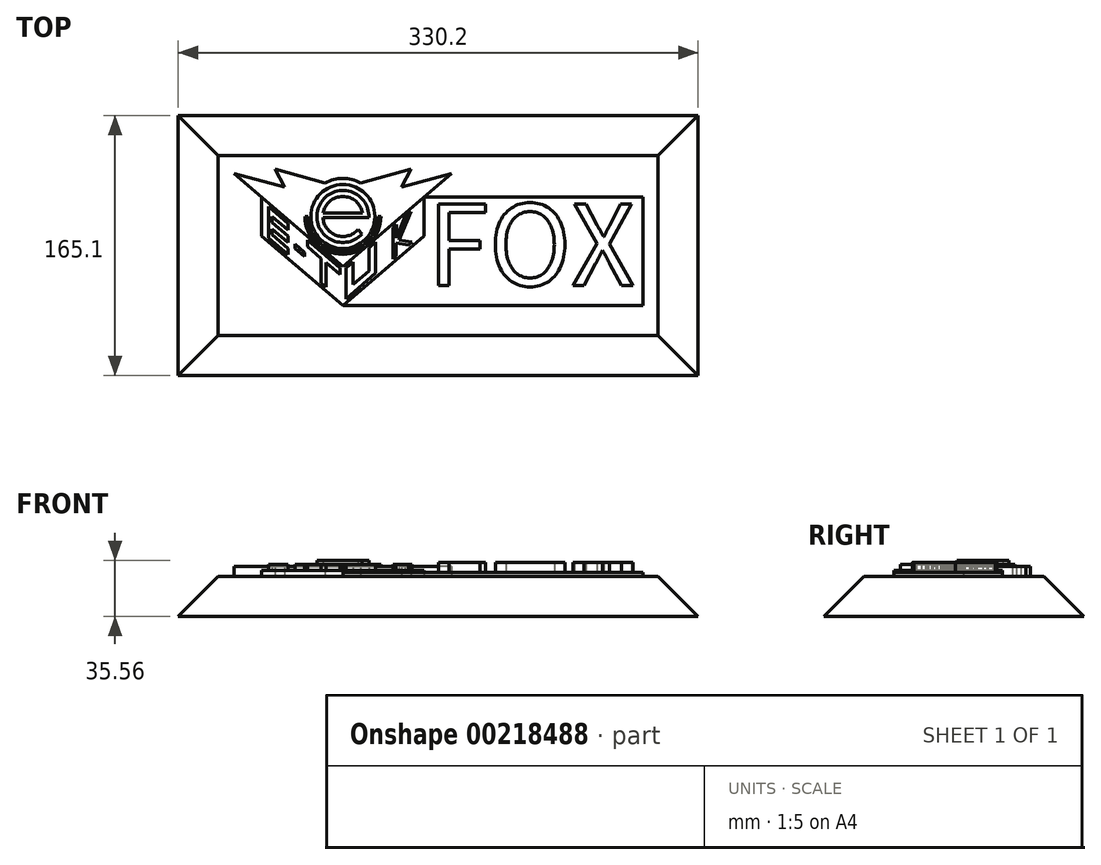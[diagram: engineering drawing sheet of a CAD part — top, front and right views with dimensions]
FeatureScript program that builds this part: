
annotation { "Feature Type Name" : "Feature", "Feature Type Description" : "" }
export const myFeature = defineFeature(function(context is Context, id is Id, definition is map)
    precondition{}
    {
        {
            var Q0;
            Q0=qCreatedBy(makeId("Top.planeOp"),FACE);
            var sketch = newSketch(context, id + "F0", { "sketchPlane" : qUnion([Q0])});
            skArc(sketch, "E0", {"start": v(12.53, 2.07) * mm, "mid": v(0, 12.7) * mm, "end": v(-12.53, 2.07) * mm});
            skArc(sketch, "E1", {"start": v(16.5, -0.78) * mm, "mid": v(-15.23, 6.37) * mm, "end": v(12.14, -11.18) * mm});
            skLineSegment(sketch, "E2", {"start": v(12.7, -0.78) * mm, "end": v(-12.68, -0.78) * mm});
            skLineSegment(sketch, "E3", {"start": v(-12.68, -0.78) * mm, "end": v(16.5, -0.78) * mm});
            skLineSegment(sketch, "E4", {"start": v(9.59, -8.33) * mm, "end": v(12.14, -11.18) * mm});
            skArc(sketch, "E5.trimOffspring", {"start": v(-12.68, -0.78) * mm, "mid": v(-4.08, -12.03) * mm, "end": v(9.59, -8.33) * mm});
            skLineSegment(sketch, "E6", {"start": v(-12.53, 2.07) * mm, "end": v(12.53, 2.07) * mm});
            skSolve(sketch);
        }
        {
            var Q0;
            Q0=makeQuery(id+"F0.imprint","IMPRINT",FACE,{"disambiguationData":[TD([[makeQuery(id+"F0.imprint","IMPRINT",EDGE,{"derivedFrom":sQuery(id+"F0.wireOp",EDGE,"E0")}),-1.0]])]});
            extrude(context, id + "F1", {"entities" : qUnion([Q0]), "depth" : 10.16 * mm});
        }
        {
            var Q0;
            Q0=qCreatedBy(makeId("Top.planeOp"),FACE);
            var sketch = newSketch(context, id + "F2", { "sketchPlane" : qUnion([Q0])});
            skCircle(sketch, "E7", {"center": v(0, 0) * mm, "radius": 20.32 * mm});
            skSolve(sketch);
        }
        {
            var Q0;
            Q0=qSketchRegion(id+"F2",true);
            extrude(context, id + "F3", {"entities" : qUnion([Q0]), "operationType" : NewBodyOperationType.ADD, "depth" : 7.62 * mm});
        }
        {
            var Q0;
            Q0=qCreatedBy(makeId("Top.planeOp"),FACE);
            var sketch = newSketch(context, id + "F4", { "sketchPlane" : qUnion([Q0])});
            skLineSegment(sketch, "E8", {"start": v(-69.02, 27.27) * mm, "end": v(-37.13, 18.72) * mm});
            skLineSegment(sketch, "E9", {"start": v(-37.13, 18.72) * mm, "end": v(-43.14, 30.14) * mm});
            skLineSegment(sketch, "E10", {"start": v(-43.14, 30.14) * mm, "end": v(-11.32, 21.31) * mm});
            skLineSegment(sketch, "E11", {"start": v(-69.02, 27.27) * mm, "end": v(0, -31.75) * mm});
            skLineSegment(sketch, "E12.MirrorCS", {"start": v(43.14, 30.14) * mm, "end": v(11.32, 21.31) * mm});
            skLineSegment(sketch, "E13.MirrorCS", {"start": v(69.02, 27.27) * mm, "end": v(0, -31.75) * mm});
            skLineSegment(sketch, "E14.MirrorCS", {"start": v(69.02, 27.27) * mm, "end": v(37.13, 18.72) * mm});
            skLineSegment(sketch, "E15.MirrorCS", {"start": v(37.13, 18.72) * mm, "end": v(43.14, 30.14) * mm});
            skArc(sketch, "E16.trimOffspring", {"start": v(11.32, 21.31) * mm, "mid": v(0, 24.13) * mm, "end": v(-11.32, 21.31) * mm});
            skSolve(sketch);
        }
        {
            var Q0;
            Q0=qSketchRegion(id+"F4",true);
            var Q1;
            Q1=makeQuery(id+"F2.imprint","IMPRINT",FACE,{"disambiguationData":[TD([[makeQuery(id+"F2.imprint","IMPRINT",EDGE,{"derivedFrom":sQuery(id+"F2.wireOp",EDGE,"E7")}),1.0]])]});
            extrude(context, id + "F5", {"entities" : qUnion([Q0, Q1]), "operationType" : NewBodyOperationType.ADD, "depth" : 6.35 * mm});
        }
        {
            var Q0;
            Q0=qCreatedBy(makeId("Top.planeOp"),FACE);
            var sketch = newSketch(context, id + "F6", { "sketchPlane" : qUnion([Q0])});
            skLineSegment(sketch, "E17", {"start": v(-51.6, -12.38) * mm, "end": v(0, -56.51) * mm});
            skLineSegment(sketch, "E18", {"start": v(0, -56.51) * mm, "end": v(51.6, -12.38) * mm});
            skLineSegment(sketch, "E19", {"start": v(-51.6, 12.38) * mm, "end": v(-51.6, -12.38) * mm});
            skLineSegment(sketch, "E20", {"start": v(51.6, 12.38) * mm, "end": v(51.6, -12.38) * mm});
            skLineSegment(sketch, "E21", {"start": v(-51.6, 12.38) * mm, "end": v(0, -31.75) * mm});
            skLineSegment(sketch, "E22", {"start": v(0, -31.75) * mm, "end": v(51.6, 12.38) * mm});
            skSolve(sketch);
        }
        {
            var Q0;
            Q0=qSketchRegion(id+"F6",true);
            extrude(context, id + "F7", {"entities" : qUnion([Q0]), "operationType" : NewBodyOperationType.ADD, "depth" : 3.8 * mm});
        }
        {
            var Q0;
            Q0=makeQuery(id+"F7.opExtrude","CAP_FACE",FACE,{"disambiguationData":[OSD([sQuery(id+"F6.wireOp",EDGE,"E17"),sQuery(id+"F6.wireOp",EDGE,"E18"),sQuery(id+"F6.wireOp",EDGE,"E19"),sQuery(id+"F6.wireOp",EDGE,"E20"),sQuery(id+"F6.wireOp",EDGE,"E21"),sQuery(id+"F6.wireOp",EDGE,"E22")])],"isStart":false});
            var sketch = newSketch(context, id + "F8", { "sketchPlane" : qUnion([Q0])});
            skPoint(sketch, "E23.startSnap0", {"position": v(-51.6, 0) * mm});
            skLineSegment(sketch, "E24", {"start": v(-51.6, -9.87) * mm, "end": v(-51.6, 9.87) * mm, "construction": true});
            skLineSegment(sketch, "E25", {"start": v(-47.26, 6.16) * mm, "end": v(-34.74, -4.55) * mm});
            skLineSegment(sketch, "E26", {"start": v(-34.74, -4.55) * mm, "end": v(-34.74, -8.63) * mm});
            skLineSegment(sketch, "E27", {"start": v(-34.74, -8.63) * mm, "end": v(-44.83, 0) * mm});
            skLineSegment(sketch, "E28", {"start": v(-44.83, 0) * mm, "end": v(-44.83, -3.75) * mm});
            skLineSegment(sketch, "E29", {"start": v(-44.83, -3.75) * mm, "end": v(-34.74, -12.38) * mm});
            skLineSegment(sketch, "E30", {"start": v(-34.74, -12.38) * mm, "end": v(-34.74, -16.46) * mm});
            skLineSegment(sketch, "E31", {"start": v(-34.74, -16.46) * mm, "end": v(-44.83, -7.83) * mm});
            skLineSegment(sketch, "E32", {"start": v(-44.83, -7.83) * mm, "end": v(-44.83, -11.58) * mm});
            skLineSegment(sketch, "E33", {"start": v(-44.83, -11.58) * mm, "end": v(-34.74, -20.21) * mm});
            skLineSegment(sketch, "E34", {"start": v(-34.74, -20.21) * mm, "end": v(-34.74, -24.3) * mm});
            skLineSegment(sketch, "E35", {"start": v(-34.74, -24.3) * mm, "end": v(-47.26, -13.59) * mm});
            skLineSegment(sketch, "E36", {"start": v(-47.26, 6.16) * mm, "end": v(-47.26, -13.59) * mm});
            skLineSegment(sketch, "E37", {"start": v(-30.38, -20.21) * mm, "end": v(-30.38, -17.65) * mm});
            skLineSegment(sketch, "E38", {"start": v(-30.38, -17.65) * mm, "end": v(-24.17, -22.96) * mm});
            skLineSegment(sketch, "E39", {"start": v(-24.17, -22.96) * mm, "end": v(-24.17, -25.53) * mm});
            skLineSegment(sketch, "E40", {"start": v(-24.17, -25.53) * mm, "end": v(-30.38, -20.21) * mm});
            skLineSegment(sketch, "E41", {"start": v(-22.38, -15.12) * mm, "end": v(-1.9, -32.63) * mm});
            skLineSegment(sketch, "E42", {"start": v(-1.9, -32.63) * mm, "end": v(-1.9, -36.71) * mm});
            skLineSegment(sketch, "E43", {"start": v(-1.9, -36.71) * mm, "end": v(-10.6, -29.28) * mm});
            skLineSegment(sketch, "E44", {"start": v(-10.6, -29.28) * mm, "end": v(-10.6, -44.95) * mm});
            skLineSegment(sketch, "E45", {"start": v(-10.6, -44.95) * mm, "end": v(-13.7, -42.3) * mm});
            skLineSegment(sketch, "E46", {"start": v(-13.7, -42.3) * mm, "end": v(-13.7, -26.63) * mm});
            skLineSegment(sketch, "E47", {"start": v(-13.7, -26.63) * mm, "end": v(-22.38, -19.2) * mm});
            skLineSegment(sketch, "E48", {"start": v(-22.38, -19.2) * mm, "end": v(-22.38, -15.12) * mm});
            skLineSegment(sketch, "E49", {"start": v(1.9, -32.62) * mm, "end": v(6.3, -28.86) * mm});
            skLineSegment(sketch, "E50", {"start": v(6.3, -28.86) * mm, "end": v(6.3, -43.26) * mm});
            skLineSegment(sketch, "E51", {"start": v(6.3, -43.26) * mm, "end": v(16.5, -34.54) * mm});
            skLineSegment(sketch, "E52", {"start": v(16.5, -34.54) * mm, "end": v(16.5, -20.14) * mm});
            skLineSegment(sketch, "E53", {"start": v(16.5, -20.14) * mm, "end": v(20.85, -16.3) * mm});
            skLineSegment(sketch, "E54", {"start": v(20.85, -16.3) * mm, "end": v(20.85, -36.06) * mm});
            skLineSegment(sketch, "E55", {"start": v(20.85, -36.06) * mm, "end": v(1.9, -52.37) * mm});
            skLineSegment(sketch, "E56", {"start": v(1.9, -52.37) * mm, "end": v(1.9, -32.62) * mm});
            skLineSegment(sketch, "E57", {"start": v(31.73, -7.12) * mm, "end": v(31.73, -27.15) * mm});
            skLineSegment(sketch, "E58", {"start": v(31.73, -27.15) * mm, "end": v(33.91, -25.22) * mm});
            skLineSegment(sketch, "E59", {"start": v(33.91, -25.22) * mm, "end": v(33.91, -16.82) * mm});
            skLineSegment(sketch, "E60", {"start": v(33.94, -13.64) * mm, "end": v(33.94, -5.23) * mm});
            skLineSegment(sketch, "E61", {"start": v(33.94, -5.23) * mm, "end": v(31.73, -7.12) * mm});
            skLineSegment(sketch, "E62", {"start": v(41.79, -18.27) * mm, "end": v(44, -16.38) * mm});
            skLineSegment(sketch, "E63", {"start": v(33.94, -13.64) * mm, "end": v(39.5, 0) * mm});
            skLineSegment(sketch, "E64", {"start": v(33.91, -16.82) * mm, "end": v(41.79, -18.27) * mm});
            skLineSegment(sketch, "E65", {"start": v(44, -16.38) * mm, "end": v(35.85, -14.87) * mm});
            skLineSegment(sketch, "E66", {"start": v(35.85, -14.87) * mm, "end": v(43.2, 3.16) * mm});
            skLineSegment(sketch, "E67", {"start": v(39.5, 0) * mm, "end": v(43.2, 3.16) * mm});
            skSolve(sketch);
        }
        {
            var Q0;
            Q0=qSketchRegion(id+"F8",true);
            extrude(context, id + "F9", {"entities" : qUnion([Q0]), "operationType" : NewBodyOperationType.ADD, "depth" : 3.8 * mm});
        }
        {
            var Q0;
            Q0=makeQuery(id+"F5.boolean.opBoolean","MERGE",FACE,{"derivedFrom":[makeQuery(id+"F5.opExtrude","CAP_FACE",FACE,{"disambiguationData":[OSD([sQuery(id+"F2.wireOp",EDGE,"E7")])],"isStart":false}),makeQuery(id+"F5.opExtrude","CAP_FACE",FACE,{"disambiguationData":[OSD([sQuery(id+"F4.wireOp",EDGE,"E8"),sQuery(id+"F4.wireOp",EDGE,"E9"),sQuery(id+"F4.wireOp",EDGE,"E10"),sQuery(id+"F4.wireOp",EDGE,"E11"),sQuery(id+"F4.wireOp",EDGE,"E13.MirrorCS"),sQuery(id+"F4.wireOp",EDGE,"E14.MirrorCS"),sQuery(id+"F4.wireOp",EDGE,"E12.MirrorCS"),sQuery(id+"F4.wireOp",EDGE,"E15.MirrorCS"),sQuery(id+"F4.wireOp",EDGE,"E16.trimOffspring")])],"isStart":false})]});
            var sketch = newSketch(context, id + "F10", { "sketchPlane" : qUnion([Q0])});
            skArc(sketch, "E68", {"start": v(-24.13, 0) * mm, "mid": v(0, -24.13) * mm, "end": v(24.13, 0) * mm});
            skArc(sketch, "E69", {"start": v(-22.23, 0) * mm, "mid": v(0, -22.23) * mm, "end": v(22.23, 0) * mm});
            skLineSegment(sketch, "E70", {"start": v(-24.13, 0) * mm, "end": v(-22.23, 0) * mm});
            skLineSegment(sketch, "E71", {"start": v(24.13, 0) * mm, "end": v(22.23, 0) * mm});
            skSolve(sketch);
        }
        {
            var Q0;
            Q0=qSketchRegion(id+"F10",true);
            extrude(context, id + "F11", {"entities" : qUnion([Q0]), "operationType" : NewBodyOperationType.ADD, "depth" : 1.27 * mm});
        }
        {
            var Q0;
            {var subQ0=sQuery(id+"F2.wireOp",EDGE,"E7");Q0=makeQuery(id+"F7.boolean.opBoolean","MERGE",FACE,{"derivedFrom":[makeQuery(id+"F5.boolean.opBoolean","MERGE",FACE,{"derivedFrom":[makeQuery(id+"F3.boolean.opBoolean","MERGE",FACE,{"derivedFrom":[makeQuery(id+"F1.opExtrude","CAP_FACE",FACE,{"disambiguationData":[OSD([sQuery(id+"F0.wireOp",EDGE,"E0"),sQuery(id+"F0.wireOp",EDGE,"E1"),sQuery(id+"F0.wireOp",EDGE,"E3"),sQuery(id+"F0.wireOp",EDGE,"E4"),sQuery(id+"F0.wireOp",EDGE,"E5.trimOffspring"),sQuery(id+"F0.wireOp",EDGE,"E6")])],"isStart":true}),makeQuery(id+"F3.opExtrude","CAP_FACE",FACE,{"disambiguationData":[OSD([subQ0])],"isStart":true})]}),makeQuery(id+"F5.opExtrude","CAP_FACE",FACE,{"disambiguationData":[OSD([subQ0])],"isStart":true}),makeQuery(id+"F5.opExtrude","CAP_FACE",FACE,{"disambiguationData":[OSD([sQuery(id+"F4.wireOp",EDGE,"E8"),sQuery(id+"F4.wireOp",EDGE,"E9"),sQuery(id+"F4.wireOp",EDGE,"E10"),sQuery(id+"F4.wireOp",EDGE,"E11"),sQuery(id+"F4.wireOp",EDGE,"E13.MirrorCS"),sQuery(id+"F4.wireOp",EDGE,"E14.MirrorCS"),sQuery(id+"F4.wireOp",EDGE,"E12.MirrorCS"),sQuery(id+"F4.wireOp",EDGE,"E15.MirrorCS"),sQuery(id+"F4.wireOp",EDGE,"E16.trimOffspring")])],"isStart":true})]}),makeQuery(id+"F7.opExtrude","CAP_FACE",FACE,{"disambiguationData":[OSD([sQuery(id+"F6.wireOp",EDGE,"E17"),sQuery(id+"F6.wireOp",EDGE,"E18"),sQuery(id+"F6.wireOp",EDGE,"E19"),sQuery(id+"F6.wireOp",EDGE,"E20"),sQuery(id+"F6.wireOp",EDGE,"E21"),sQuery(id+"F6.wireOp",EDGE,"E22")])],"isStart":true})]});}
            var sketch = newSketch(context, id + "F12", { "sketchPlane" : qUnion([Q0])});
            skLineSegment(sketch, "E72.bottom", {"start": v(0, 56.51) * mm, "end": v(190.5, 56.51) * mm});
            skLineSegment(sketch, "E72.right", {"start": v(190.5, 56.51) * mm, "end": v(190.5, -12.38) * mm});
            skLineSegment(sketch, "E73", {"start": v(51.6, -12.38) * mm, "end": v(190.5, -12.38) * mm});
            skLineSegment(sketch, "E74", {"start": v(0, 56.51) * mm, "end": v(51.6, 12.38) * mm});
            skLineSegment(sketch, "E75", {"start": v(51.6, 12.38) * mm, "end": v(51.6, -12.38) * mm});
            skSolve(sketch);
        }
        {
            var Q0;
            Q0=qSketchRegion(id+"F12",true);
            extrude(context, id + "F13", {"entities" : qUnion([Q0]), "operationType" : NewBodyOperationType.ADD, "oppositeDirection" : true, "depth" : 2.54 * mm});
        }
        {
            var Q0;
            Q0=makeQuery(id+"F13.opExtrude","CAP_FACE",FACE,{"disambiguationData":[OSD([sQuery(id+"F12.wireOp",EDGE,"E72.bottom"),sQuery(id+"F12.wireOp",EDGE,"E72.right"),sQuery(id+"F12.wireOp",EDGE,"E73"),sQuery(id+"F12.wireOp",EDGE,"E74"),sQuery(id+"F12.wireOp",EDGE,"E75")])],"isStart":false});
            var sketch = newSketch(context, id + "F14", { "sketchPlane" : qUnion([Q0])});
            skText(sketch, "E76", { "text": "FOX", "fontName": "NotoSansCJKkr-Regular.otf"});
            const initialGuessF14  = {"E76": [0.05376, -0.04386, 1, 0, 0.0508]};
            skSetInitialGuess(sketch, initialGuessF14);
            skSolve(sketch);
        }
        {
            var Q0;
            Q0=qSketchRegion(id+"F14",true);
            extrude(context, id + "F15", {"entities" : qUnion([Q0]), "operationType" : NewBodyOperationType.ADD, "depth" : 6.35 * mm});
        }
        {
            var Q0;
            {var subQ0=sQuery(id+"F2.wireOp",EDGE,"E7");Q0=makeQuery(id+"F13.boolean.opBoolean","MERGE",FACE,{"derivedFrom":[makeQuery(id+"F7.boolean.opBoolean","MERGE",FACE,{"derivedFrom":[makeQuery(id+"F5.boolean.opBoolean","MERGE",FACE,{"derivedFrom":[makeQuery(id+"F3.boolean.opBoolean","MERGE",FACE,{"derivedFrom":[makeQuery(id+"F1.opExtrude","CAP_FACE",FACE,{"disambiguationData":[OSD([sQuery(id+"F0.wireOp",EDGE,"E0"),sQuery(id+"F0.wireOp",EDGE,"E1"),sQuery(id+"F0.wireOp",EDGE,"E3"),sQuery(id+"F0.wireOp",EDGE,"E4"),sQuery(id+"F0.wireOp",EDGE,"E5.trimOffspring"),sQuery(id+"F0.wireOp",EDGE,"E6")])],"isStart":true}),makeQuery(id+"F3.opExtrude","CAP_FACE",FACE,{"disambiguationData":[OSD([subQ0])],"isStart":true})]}),makeQuery(id+"F5.opExtrude","CAP_FACE",FACE,{"disambiguationData":[OSD([subQ0])],"isStart":true}),makeQuery(id+"F5.opExtrude","CAP_FACE",FACE,{"disambiguationData":[OSD([sQuery(id+"F4.wireOp",EDGE,"E8"),sQuery(id+"F4.wireOp",EDGE,"E9"),sQuery(id+"F4.wireOp",EDGE,"E10"),sQuery(id+"F4.wireOp",EDGE,"E11"),sQuery(id+"F4.wireOp",EDGE,"E13.MirrorCS"),sQuery(id+"F4.wireOp",EDGE,"E14.MirrorCS"),sQuery(id+"F4.wireOp",EDGE,"E12.MirrorCS"),sQuery(id+"F4.wireOp",EDGE,"E15.MirrorCS"),sQuery(id+"F4.wireOp",EDGE,"E16.trimOffspring")])],"isStart":true})]}),makeQuery(id+"F7.opExtrude","CAP_FACE",FACE,{"disambiguationData":[OSD([sQuery(id+"F6.wireOp",EDGE,"E17"),sQuery(id+"F6.wireOp",EDGE,"E18"),sQuery(id+"F6.wireOp",EDGE,"E19"),sQuery(id+"F6.wireOp",EDGE,"E20"),sQuery(id+"F6.wireOp",EDGE,"E21"),sQuery(id+"F6.wireOp",EDGE,"E22")])],"isStart":true})]}),makeQuery(id+"F13.opExtrude","CAP_FACE",FACE,{"disambiguationData":[OSD([sQuery(id+"F12.wireOp",EDGE,"E72.bottom"),sQuery(id+"F12.wireOp",EDGE,"E72.right"),sQuery(id+"F12.wireOp",EDGE,"E73"),sQuery(id+"F12.wireOp",EDGE,"E74"),sQuery(id+"F12.wireOp",EDGE,"E75")])],"isStart":true})]});}
            var sketch = newSketch(context, id + "F16", { "sketchPlane" : qUnion([Q0])});
            skLineSegment(sketch, "E77.bottom", {"start": v(-79.18, -38.74) * mm, "end": v(200.22, -38.74) * mm});
            skLineSegment(sketch, "E77.top", {"start": v(-79.18, 75.56) * mm, "end": v(200.22, 75.56) * mm});
            skLineSegment(sketch, "E77.left", {"start": v(-79.18, -38.74) * mm, "end": v(-79.18, 75.56) * mm});
            skLineSegment(sketch, "E77.right", {"start": v(200.22, -38.74) * mm, "end": v(200.22, 75.56) * mm});
            skSolve(sketch);
        }
        {
            var Q0;
            Q0=qSketchRegion(id+"F16",true);
            extrude(context, id + "F17", {"entities" : qUnion([Q0]), "operationType" : NewBodyOperationType.ADD, "depth" : 25.4 * mm, "hasDraft" : true, "draftAngle" : 45 * degree});
        }
    });
